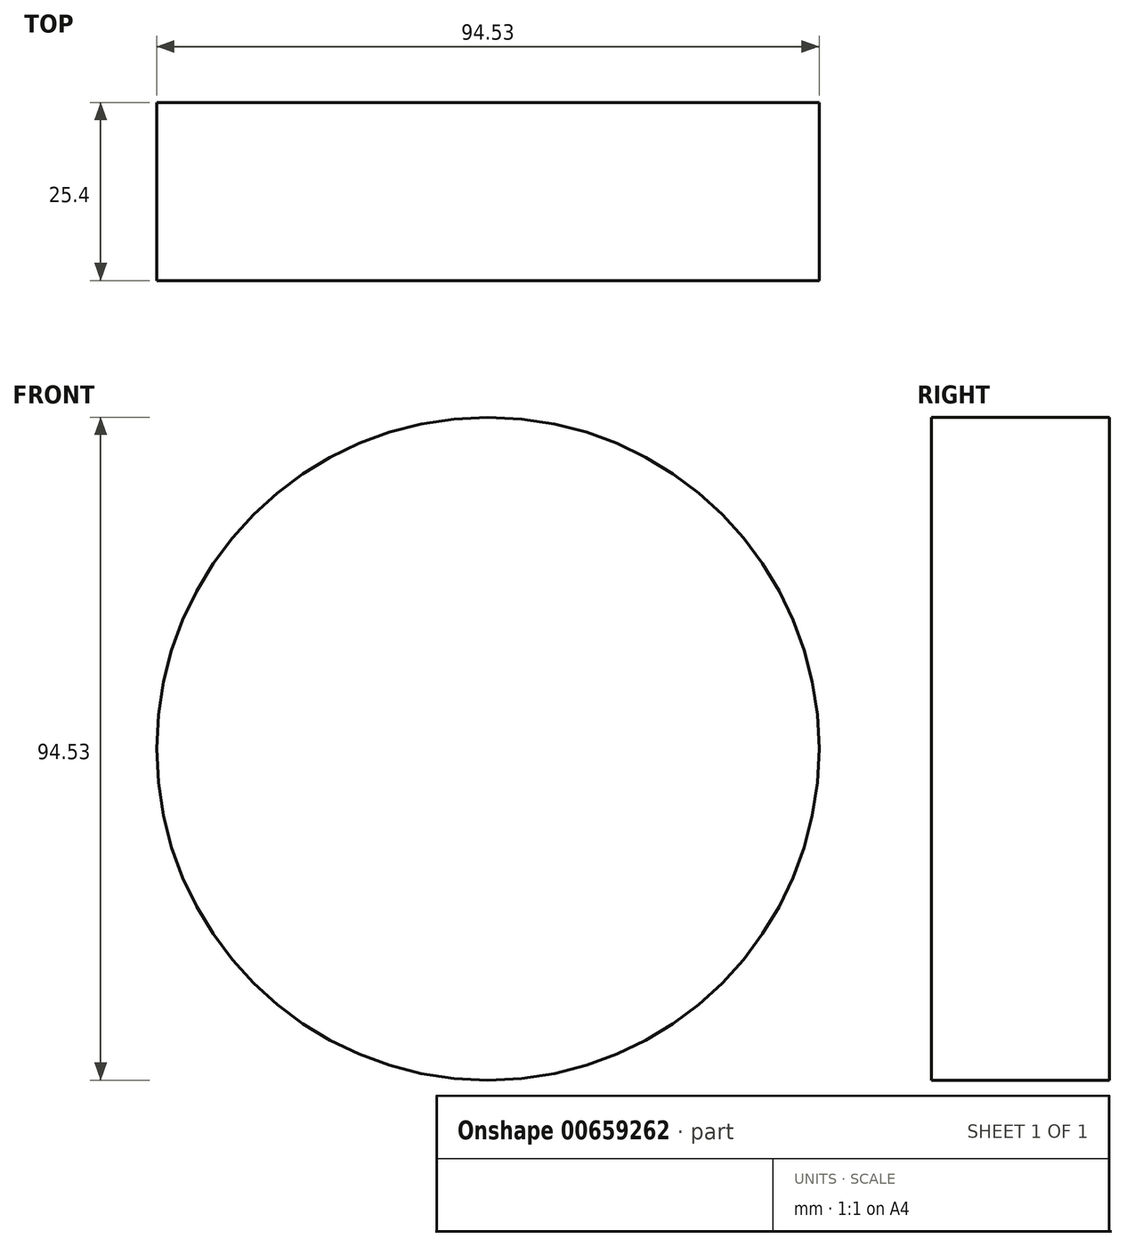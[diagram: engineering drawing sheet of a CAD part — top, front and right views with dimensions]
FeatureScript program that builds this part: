
annotation { "Feature Type Name" : "Feature", "Feature Type Description" : "" }
export const myFeature = defineFeature(function(context is Context, id is Id, definition is map)
    precondition{}
    {
        {
            var Q0;
            Q0=qCreatedBy(makeId("Front.planeOp"),FACE);
            var sketch = newSketch(context, id + "F0", { "sketchPlane" : qUnion([Q0])});
            skLineSegment(sketch, "E0.top", {"start": v(0, 99.23) * mm, "end": v(0, 99.23) * mm});
            skPoint(sketch, "E1.oppositeSnap0", {"position": v(0, -74.39) * mm});
            skCircle(sketch, "E2", {"center": v(-13.72, 11.6) * mm, "radius": 47.27 * mm});
            skSolve(sketch);
        }
        {
            var Q0;
            Q0=sQuery(id+"F0.wireOp",EDGE,"E2");
            extrude(context, id + "F1", {"bodyType" : ToolBodyType.SURFACE, "surfaceEntities" : qUnion([Q0]), "depth" : 25.4 * mm, "offsetDistance" : 25.4 * mm});
        }
    });
